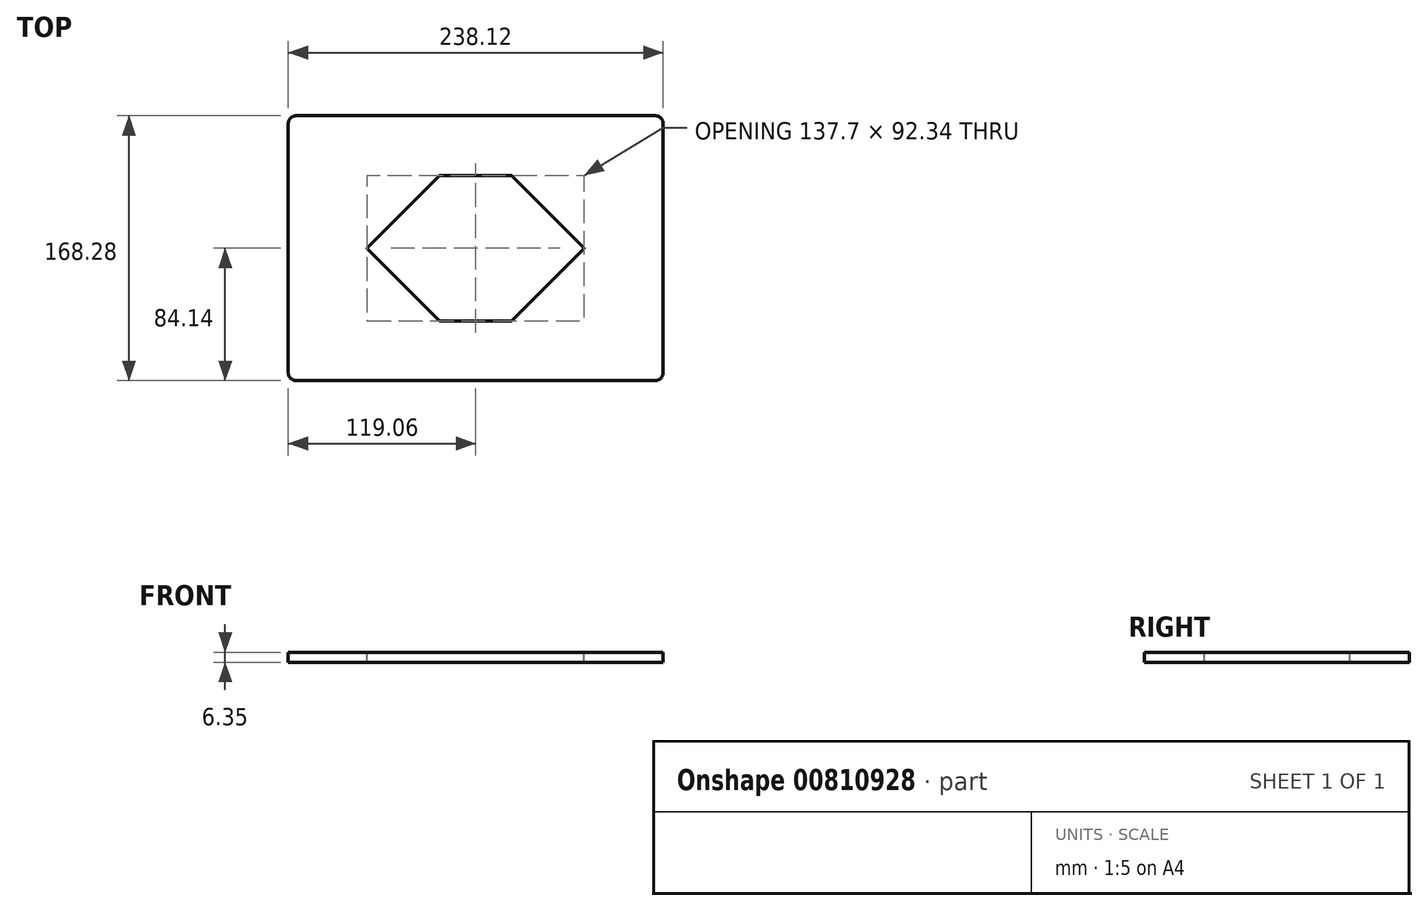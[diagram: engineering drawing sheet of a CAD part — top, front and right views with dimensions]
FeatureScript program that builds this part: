
annotation { "Feature Type Name" : "Feature", "Feature Type Description" : "" }
export const myFeature = defineFeature(function(context is Context, id is Id, definition is map)
    precondition{}
    {
        {
            var Q0;
            Q0=qCreatedBy(makeId("Top.planeOp"),FACE);
            var sketch = newSketch(context, id + "F0", { "sketchPlane" : qUnion([Q0])});
            skLineSegment(sketch, "E0.bottom", {"start": v(-119.06, 84.14) * mm, "end": v(119.06, 84.14) * mm});
            skLineSegment(sketch, "E0.top", {"start": v(-119.06, -84.14) * mm, "end": v(119.06, -84.14) * mm});
            skLineSegment(sketch, "E0.left", {"start": v(-119.06, 84.14) * mm, "end": v(-119.06, -84.14) * mm});
            skLineSegment(sketch, "E0.right", {"start": v(119.06, 84.14) * mm, "end": v(119.06, -84.14) * mm});
            skPoint(sketch, "E0.middle", {"position": v(0, 0) * mm});
            skSolve(sketch);
        }
        {
            var Q0;
            Q0 = qSketchRegion(id + "F0", true);
            extrude(context, id + "F1", {"entities" : qUnion([Q0]), "depth" : 6.35 * mm, "offsetDistance" : 25.4 * mm});
        }
        {
            var Q0;
            Q0=makeQuery(id+"F1.opExtrude","SWEPT_EDGE",EDGE,{"disambiguationData":[OSD([sQuery(id+"F0.wireOp",EDGE,"E0.bottom"),sQuery(id+"F0.wireOp",EDGE,"E0.right")])]});
            var Q1;
            Q1=makeQuery(id+"F1.opExtrude","SWEPT_EDGE",EDGE,{"disambiguationData":[OSD([sQuery(id+"F0.wireOp",EDGE,"E0.top"),sQuery(id+"F0.wireOp",EDGE,"E0.right")])]});
            var Q2;
            Q2=makeQuery(id+"F1.opExtrude","SWEPT_EDGE",EDGE,{"disambiguationData":[OSD([sQuery(id+"F0.wireOp",EDGE,"E0.top"),sQuery(id+"F0.wireOp",EDGE,"E0.left")])]});
            var Q3;
            Q3=makeQuery(id+"F1.opExtrude","SWEPT_EDGE",EDGE,{"disambiguationData":[OSD([sQuery(id+"F0.wireOp",EDGE,"E0.bottom"),sQuery(id+"F0.wireOp",EDGE,"E0.left")])]});
            fillet(context, id + "F2", {"entities" : qUnion([Q0, Q1, Q2, Q3]), "radius" : 5.08 * mm, "tangentPropagation" : true, "allowEdgeOverflow" : false});
        }
        {
            var Q0;
            Q0=makeQuery(id+"F1.opExtrude","CAP_FACE",FACE,{"disambiguationData":[OSD([sQuery(id+"F0.wireOp",EDGE,"E0.bottom"),sQuery(id+"F0.wireOp",EDGE,"E0.top"),sQuery(id+"F0.wireOp",EDGE,"E0.left"),sQuery(id+"F0.wireOp",EDGE,"E0.right")])],"isStart":false});
            var sketch = newSketch(context, id + "F3", { "sketchPlane" : qUnion([Q0])});
            skLineSegment(sketch, "E1", {"start": v(-22.48, 44.9) * mm, "end": v(22.48, 44.9) * mm});
            skLineSegment(sketch, "E2", {"start": v(22.48, 44.9) * mm, "end": v(67.38, 0) * mm});
            skLineSegment(sketch, "E3", {"start": v(-22.48, 44.9) * mm, "end": v(-67.38, 0) * mm});
            skLineSegment(sketch, "E4.MirrorCS", {"start": v(-22.48, -44.9) * mm, "end": v(-67.38, 0) * mm});
            skLineSegment(sketch, "E5.MirrorCS", {"start": v(-22.48, -44.9) * mm, "end": v(22.48, -44.9) * mm});
            skLineSegment(sketch, "E6.MirrorCS", {"start": v(22.48, -44.9) * mm, "end": v(67.38, 0) * mm});
            skSolve(sketch);
        }
        {
            var Q0;
            Q0 = qSketchRegion(id + "F3", true);
            extrude(context, id + "F4", {"entities" : qUnion([Q0]), "operationType" : NewBodyOperationType.REMOVE, "oppositeDirection" : true, "depth" : 25.4 * mm, "offsetDistance" : 25.4 * mm});
        }
        {
            var Q0;
            Q0=makeQuery(id+"F1.opExtrude","CAP_FACE",FACE,{"disambiguationData":[OSD([sQuery(id+"F0.wireOp",EDGE,"E0.bottom"),sQuery(id+"F0.wireOp",EDGE,"E0.top"),sQuery(id+"F0.wireOp",EDGE,"E0.left"),sQuery(id+"F0.wireOp",EDGE,"E0.right")])],"isStart":false});
            var sketch = newSketch(context, id + "F5", { "sketchPlane" : qUnion([Q0])});
            skLineSegment(sketch, "E7.0", {"start": v(-23, 46.17) * mm, "end": v(-69.18, 0) * mm});
            skLineSegment(sketch, "E7.1", {"start": v(23, 46.17) * mm, "end": v(69.18, 0) * mm});
            skLineSegment(sketch, "E7.2", {"start": v(23, -46.17) * mm, "end": v(69.18, 0) * mm});
            skLineSegment(sketch, "E7.3", {"start": v(-23, 46.17) * mm, "end": v(23, 46.17) * mm});
            skLineSegment(sketch, "E7.4", {"start": v(-23, -46.17) * mm, "end": v(23, -46.17) * mm});
            skLineSegment(sketch, "E7.5", {"start": v(-23, -46.17) * mm, "end": v(-69.18, 0) * mm});
            skSolve(sketch);
        }
        {
            var Q0;
            Q0 = qSketchRegion(id + "F5", true);
            extrude(context, id + "F6", {"entities" : qUnion([Q0]), "operationType" : NewBodyOperationType.REMOVE, "oppositeDirection" : true, "depth" : 25.4 * mm, "offsetDistance" : 25.4 * mm});
        }
        {
            var Q0;
            Q0=makeQuery(id+"F6.boolean.opBoolean","COPY",EDGE,{"derivedFrom":makeQuery(id+"F6.opExtrude","SWEPT_EDGE",EDGE,{"disambiguationData":[OSD([sQuery(id+"F5.wireOp",EDGE,"E7.0"),sQuery(id+"F5.wireOp",EDGE,"E7.3")])]})});
            var Q1;
            Q1=makeQuery(id+"F6.boolean.opBoolean","COPY",EDGE,{"derivedFrom":makeQuery(id+"F6.opExtrude","SWEPT_EDGE",EDGE,{"disambiguationData":[OSD([sQuery(id+"F5.wireOp",EDGE,"E7.1"),sQuery(id+"F5.wireOp",EDGE,"E7.3")])]})});
            var Q2;
            Q2=makeQuery(id+"F6.boolean.opBoolean","COPY",EDGE,{"derivedFrom":makeQuery(id+"F6.opExtrude","SWEPT_EDGE",EDGE,{"disambiguationData":[OSD([sQuery(id+"F5.wireOp",EDGE,"E7.0"),sQuery(id+"F5.wireOp",EDGE,"E7.5")])]})});
            var Q3;
            Q3=makeQuery(id+"F6.boolean.opBoolean","COPY",EDGE,{"derivedFrom":makeQuery(id+"F6.opExtrude","SWEPT_EDGE",EDGE,{"disambiguationData":[OSD([sQuery(id+"F5.wireOp",EDGE,"E7.4"),sQuery(id+"F5.wireOp",EDGE,"E7.5")])]})});
            var Q4;
            Q4=makeQuery(id+"F6.boolean.opBoolean","COPY",EDGE,{"derivedFrom":makeQuery(id+"F6.opExtrude","SWEPT_EDGE",EDGE,{"disambiguationData":[OSD([sQuery(id+"F5.wireOp",EDGE,"E7.2"),sQuery(id+"F5.wireOp",EDGE,"E7.4")])]})});
            var Q5;
            Q5=makeQuery(id+"F6.boolean.opBoolean","COPY",EDGE,{"derivedFrom":makeQuery(id+"F6.opExtrude","SWEPT_EDGE",EDGE,{"disambiguationData":[OSD([sQuery(id+"F5.wireOp",EDGE,"E7.1"),sQuery(id+"F5.wireOp",EDGE,"E7.2")])]})});
            fillet(context, id + "F7", {"entities" : qUnion([Q0, Q1, Q2, Q3, Q4, Q5]), "radius" : 0.79 * mm, "tangentPropagation" : true, "allowEdgeOverflow" : false});
        }
    });
